# Revit family: Hager-Univers-IP44-D161-Cl.II-FWB-encl--NoHosted-PL-en
name_source: partatom
category: Equipement électrique
units: mm (PartAtom-declared; Revit-internal decimal feet)

## family parameters
Basée sur le plan de construction = Oui
Configuration du panneau = Deux colonnes, circuits au sein
Cote de connecteur circulaire = Utiliser le diamètre
Couper avec des vides une fois chargée = Non
Partagée = Non
Point de calcul de pièce = Non
Toujours verticalement = Oui
Type d'élément = Tableau de raccordement

## types (19) — shared parameters
Commentaires du type = Univers
EF000003 - Mounting method = EV000384 - Surface mounted (plaster)
EF000007 - Colour = EV000202 - White
EF000049 - Depth = 161 mm  [stored 0.528215 ft]
EF000116 - RAL-number = 9010
EF000118 - With mounting plate = Non
EF001088 - Extension possible = Oui
EF001596 - Material housing = EV000179 - Steel
EF001613 - Circuit integrity = EV000494 - None
EF002950 - Width in number of modular spacings = 12
EF003532 - Suitable for outdoor use = Non
EF004293 - Impact strength = EV006815 - IK09
EF005474 - Degree of protection (IP) = EV006418 - IP44
EF006244 - Transparent cover/door = Non
EF006306 - With lock = Non
EF007800 - Suitable for lightning protection = Non
EF008873 - Nominal current (In) = 125 A
EF015940 - Cover with overpressure release = Non
Elévation par défaut = 1219 mm
Fabricant = Hager
HG000002 - With door or cover = Oui
HG000003 - Range = Univers
HG000006 - Flush mounted = Non
HG000023 - Double section enclosure = Non
HG000024 - Bottom section height = 600 mm
HG000026 - Floor standing = Non
zero-valued in all types: EF000218 - Built-in depth, EF000266 - Number of rows, HG000027 - Plinth height

## per-type parameters (varying)
| type | EF000008 - Width | EF000040 - Height | EF000339 - Type of cover | EF000437 - Number of conduit inlets | EF001131 - Internal depth | EF004427 - Number of modules | EF004464 - Type of door | EF009170 - Material plate thickness cabinet | EF009171 - Material plate thickness door/cover | EF009212 - Cover model | EF009554 - Number of openings for flange plates | HG000004 - Manufacturer reference | HG000009 - Double swing door | HG000010 - Asymmetric doors |
| Surface mounted (plaster) IP44 W1050 H1100 D161  - FWB74D | 1050 mm | 1100 mm | EV000494 - None | 16 | 160 mm  [stored 0.524934 ft] | 336 | EV000494 - None | 1 mm  [stored 0.00328084 ft] | 1 mm  [stored 0.00328084 ft] | EV000116 - Closed | 8 | FWB74D | Oui | Non |
| Surface mounted (plaster) IP44 W1050 H500 D161  - FWB34D | 1050 mm | 500 mm  [stored 1.64042 ft] | EV004216 - Door | 16 | 156 mm  [stored 0.511811 ft] | 144 | EV003602 - Double | 1 mm  [stored 0.00328084 ft] | 1 mm  [stored 0.00328084 ft] | EV000116 - Closed | 8 | FWB34D | Oui | Non |
| Surface mounted (plaster) IP44 W1050 H650 D161  - FWB44D | 1050 mm | 650 mm  [stored 2.13255 ft] | EV004216 - Door | 16 | 156 mm  [stored 0.511811 ft] | 192 | EV003602 - Double | 1 mm  [stored 0.00328084 ft] | 1 mm  [stored 0.00328084 ft] | EV000116 - Closed | 8 | FWB44D | Oui | Non |
| Surface mounted (plaster) IP44 W1050 H800 D161  - FWB54D | 1050 mm | 800 mm  [stored 2.62467 ft] | EV004216 - Door | 16 | 156 mm  [stored 0.511811 ft] | 240 | EV002646 - Single | 1 mm  [stored 0.00328084 ft] | 1 mm  [stored 0.00328084 ft] | EV000116 - Closed | 8 | FWB54D | Oui | Non |
| Surface mounted (plaster) IP44 W1050 H950 D161  - FWB64D | 1050 mm | 950 mm  [stored 3.1168 ft] | EV004216 - Door | 16 | 156 mm  [stored 0.511811 ft] | 288 | EV003602 - Double | 1 mm  [stored 0.00328084 ft] | 1 mm  [stored 0.00328084 ft] | EV000116 - Closed | 8 | FWB64D | Oui | Non |
| Surface mounted (plaster) IP44 W300 H1100 D161  - FWB71D | 300 mm | 1100 mm | EV004216 - Door | 4 | 160 mm  [stored 0.524934 ft] | 84 | EV000494 - None | 1 mm  [stored 0.00328084 ft] | 1 mm  [stored 0.00328084 ft] | EV000116 - Closed | 2 | FWB71D | Non | Non |
| Surface mounted (plaster) IP44 W300 H650 D161  - FWB41D | 300 mm | 650 mm  [stored 2.13255 ft] | EV004216 - Door | 4 | 160 mm  [stored 0.524934 ft] | 48 | EV000494 - None | 2 mm  [stored 0.00656168 ft] | 2 mm  [stored 0.00656168 ft] | EV000116 - Closed | 2 | FWB41D | Non | Non |
| Surface mounted (plaster) IP44 W300 H800 D161  - FWB51D | 300 mm | 800 mm  [stored 2.62467 ft] | EV004216 - Door | 4 | 160 mm  [stored 0.524934 ft] | 60 | EV000494 - None | 1 mm  [stored 0.00328084 ft] | 1 mm  [stored 0.00328084 ft] | EV000116 - Closed | 2 | FWB51D | Non | Non |
| Surface mounted (plaster) IP44 W300 H950 D161  - FWB61D | 300 mm | 950 mm  [stored 3.1168 ft] | EV004216 - Door | 4 | 160 mm  [stored 0.524934 ft] | 72 | EV000494 - None | 1 mm  [stored 0.00328084 ft] | 1 mm  [stored 0.00328084 ft] | EV000116 - Closed | 2 | FWB61D | Non | Non |
| Surface mounted (plaster) IP44 W550 H1100 D161  - FWB72D | 550 mm | 1100 mm | EV004216 - Door | 8 | 160 mm  [stored 0.524934 ft] | 168 | EV000494 - None | 1 mm  [stored 0.00328084 ft] | 1 mm  [stored 0.00328084 ft] | EV000116 - Closed | 4 | FWB72D | Non | Non |
| Surface mounted (plaster) IP44 W550 H500 D161  - FWB32D | 550 mm | 500 mm  [stored 1.64042 ft] | EV000494 - None | 8 | 156 mm  [stored 0.511811 ft] | 72 | EV002646 - Single | 2 mm  [stored 0.00656168 ft] | 2 mm  [stored 0.00656168 ft] | EV000116 - Closed | 4 | FWB32D | Non | Non |
| Surface mounted (plaster) IP44 W550 H650 D161  - FWB42D | 550 mm | 650 mm  [stored 2.13255 ft] | EV004216 - Door | 8 | 160 mm  [stored 0.524934 ft] | 96 | EV000494 - None | 1 mm  [stored 0.00328084 ft] | 1 mm  [stored 0.00328084 ft] | EV000116 - Closed | 4 | FWB42D | Non | Non |
| Surface mounted (plaster) IP44 W550 H800 D161  - FWB52D | 550 mm | 800 mm  [stored 2.62467 ft] | EV004216 - Door | 8 | 160 mm  [stored 0.524934 ft] | 120 | EV000494 - None | 1 mm  [stored 0.00328084 ft] | 1 mm  [stored 0.00328084 ft] | EV000116 - Closed | 4 | FWB52D | Non | Non |
| Surface mounted (plaster) IP44 W550 H950 D161  - FWB62D | 550 mm | 950 mm  [stored 3.1168 ft] | EV004216 - Door | 8 | 160 mm  [stored 0.524934 ft] | 144 | EV000494 - None | 1 mm  [stored 0.00328084 ft] | 1 mm  [stored 0.00328084 ft] | EV000116 - Closed | 4 | FWB62D | Non | Non |
| Surface mounted (plaster) IP44 W800 H1100 D161  - FWB73D | 800 mm  [stored 2.62467 ft] | 1100 mm | EV004216 - Door | 12 | 156 mm  [stored 0.511811 ft] | 252 | EV003602 - Double | 1 mm  [stored 0.00328084 ft] | 1 mm  [stored 0.00328084 ft] | EV000116 - Closed | 6 | FWB73D | Oui | Oui |
| Surface mounted (plaster) IP44 W800 H500 D161  - FWB33D | 800 mm  [stored 2.62467 ft] | 500 mm  [stored 1.64042 ft] | EV004216 - Door | 12 | 160 mm  [stored 0.524934 ft] | 108 | EV000494 - None | 1 mm  [stored 0.00328084 ft] | 1 mm  [stored 0.00328084 ft] | EV000116 - Closed | 6 | FWB33D | Oui | Oui |
| Surface mounted (plaster) IP44 W800 H650 D161  - FWB43D | 800 mm  [stored 2.62467 ft] | 650 mm  [stored 2.13255 ft] | EV004216 - Door | 12 | 160 mm  [stored 0.524934 ft] | 144 | EV000494 - None | 2 mm  [stored 0.00656168 ft] | 1 mm  [stored 0.00328084 ft] | EV009916 - With notch | 6 | FWB43D | Oui | Oui |
| Surface mounted (plaster) IP44 W800 H800 D161  - FWB53D | 800 mm  [stored 2.62467 ft] | 800 mm  [stored 2.62467 ft] | EV004216 - Door | 12 | 160 mm  [stored 0.524934 ft] | 180 | EV000494 - None | 2 mm  [stored 0.00656168 ft] | 1 mm  [stored 0.00328084 ft] | EV000116 - Closed | 6 | FWB53D | Oui | Oui |
| Surface mounted (plaster) IP44 W800 H950 D161  - FWB63D | 800 mm  [stored 2.62467 ft] | 950 mm  [stored 3.1168 ft] | EV004216 - Door | 12 | 156 mm  [stored 0.511811 ft] | 216 | EV000494 - None | 1 mm  [stored 0.00328084 ft] | 1 mm  [stored 0.00328084 ft] | EV000116 - Closed | 6 | FWB63D | Oui | Oui |

note: [stored X ft] marks values corroborated as IEEE doubles in the binary element streams (Revit-internal decimal feet)

## geometry (parser evidence)
native form markers: Blend x4, Sweep x10
no freeform markers — native parametric forms only
